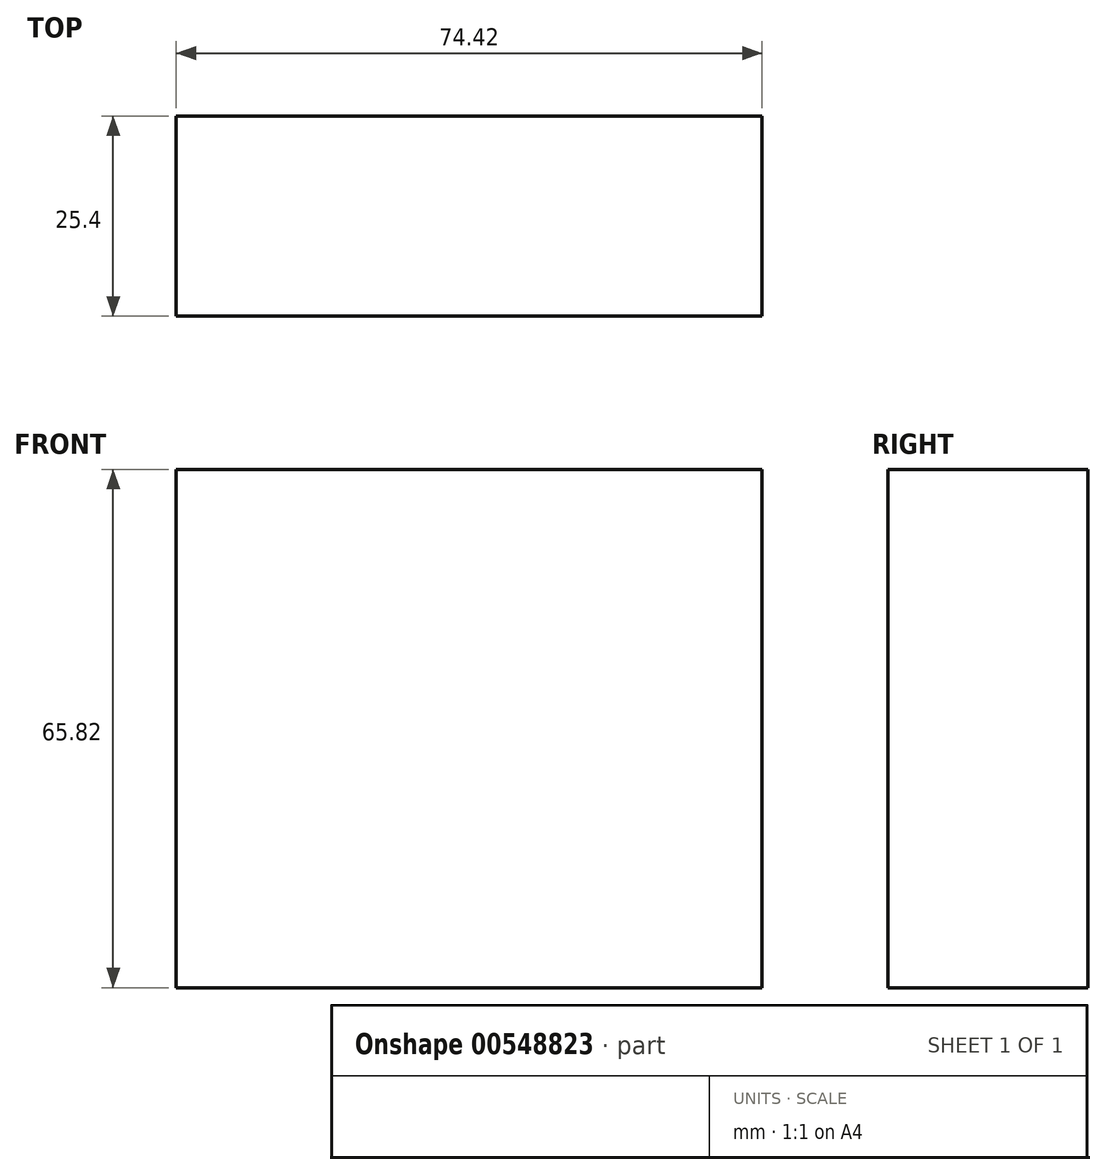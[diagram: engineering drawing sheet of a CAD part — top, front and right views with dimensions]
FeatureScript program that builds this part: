
annotation { "Feature Type Name" : "Feature", "Feature Type Description" : "" }
export const myFeature = defineFeature(function(context is Context, id is Id, definition is map)
    precondition{}
    {
        {
            var Q0;
            Q0=qCreatedBy(makeId("Front.planeOp"),FACE);
            var sketch = newSketch(context, id + "F0", { "sketchPlane" : qUnion([Q0])});
            skLineSegment(sketch, "E0.bottom", {"start": v(-19.14, 45.64) * mm, "end": v(55.28, 45.64) * mm});
            skLineSegment(sketch, "E0.top", {"start": v(-19.14, -20.18) * mm, "end": v(55.28, -20.18) * mm});
            skLineSegment(sketch, "E0.left", {"start": v(-19.14, 45.64) * mm, "end": v(-19.14, -20.18) * mm});
            skLineSegment(sketch, "E0.right", {"start": v(55.28, 45.64) * mm, "end": v(55.28, -20.18) * mm});
            skSolve(sketch);
        }
        {
            var Q0;
            Q0 = qSketchRegion(id + "F0", true);
            extrude(context, id + "F1", {"entities" : qUnion([Q0]), "depth" : 25.4 * mm, "offsetDistance" : 25.4 * mm});
        }
    });
